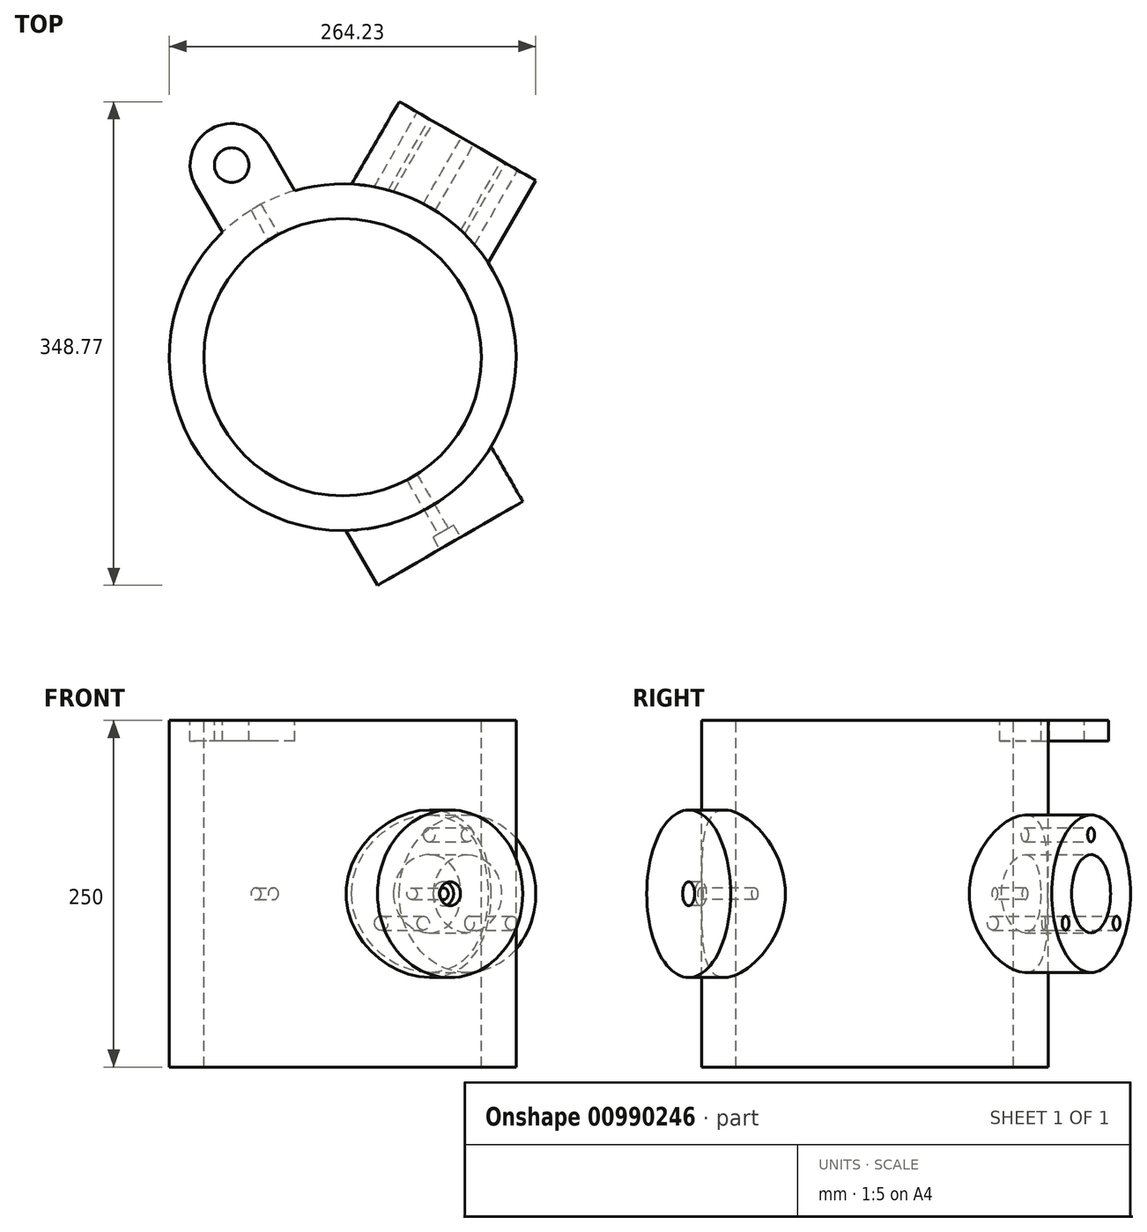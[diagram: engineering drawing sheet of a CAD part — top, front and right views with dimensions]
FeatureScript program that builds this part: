
annotation { "Feature Type Name" : "Feature", "Feature Type Description" : "" }
export const myFeature = defineFeature(function(context is Context, id is Id, definition is map)
    precondition{}
    {
        {
            var Q0;
            Q0=qCreatedBy(makeId("Top.planeOp"),FACE);
            cPlane(context, id + "F0", {"entities" : qUnion([Q0]), "cplaneType" : CPlaneType.OFFSET, "offset" : 125 * mm, "width" : 150 * mm, "height" : 150 * mm});
        }
        {
            var Q0;
            Q0=qCreatedBy(id+"F0.planeOp",FACE);
            var sketch = newSketch(context, id + "F1", { "sketchPlane" : qUnion([Q0])});
            skCircle(sketch, "E0", {"center": v(0, 0) * mm, "radius": 125 * mm});
            skCircle(sketch, "E1", {"center": v(0, 0) * mm, "radius": 100 * mm});
            skCircle(sketch, "E2", {"center": v(0, 0) * mm, "radius": 160 * mm, "construction": true});
            skSolve(sketch);
        }
        {
            var Q0;
            Q0 = qSketchRegion(id + "F1", true);
            extrude(context, id + "F2", {"entities" : qUnion([Q0]), "oppositeDirection" : true, "depth" : 250 * mm, "offsetDistance" : 25 * mm});
        }
        {
            var Q0;
            Q0=makeQuery(id+"F1.imprint","IMPRINT",FACE,{"disambiguationData":[TD([[makeQuery(id+"F1.imprint","IMPRINT",EDGE,{"derivedFrom":sQuery(id+"F1.wireOp",EDGE,"E0")}),1.0]])]});
            var sketch = newSketch(context, id + "F3", { "sketchPlane" : qUnion([Q0])});
            skLineSegment(sketch, "E3", {"start": v(0, 0) * mm, "end": v(-100, -173.2) * mm, "construction": true});
            skLineSegment(sketch, "E4", {"start": v(0, 0) * mm, "end": v(-105.59, 182.88) * mm, "construction": true});
            skLineSegment(sketch, "E5", {"start": v(0, 0) * mm, "end": v(211.08, 0) * mm, "construction": true});
            skLineSegment(sketch, "E6", {"start": v(-86.65, 90.09) * mm, "end": v(-105.98, 123.56) * mm});
            skArc(sketch, "E7", {"start": v(-105.98, 123.56) * mm, "mid": v(-94.98, 164.56) * mm, "end": v(-54, 153.53) * mm});
            skLineSegment(sketch, "E8.MirrorCS", {"start": v(-34.7, 120.09) * mm, "end": v(-54.02, 153.56) * mm});
            skCircle(sketch, "E9", {"center": v(-80, 138.56) * mm, "radius": 12.5 * mm});
            skLineSegment(sketch, "E10", {"start": v(0, 0) * mm, "end": v(-199.04, 0) * mm, "construction": true});
            skSolve(sketch);
        }
        {
            var Q0;
            {var subQ4=sQuery(id+"F3.wireOp",EDGE,"E6");Q0=makeQuery(id+"F3.imprint","IMPRINT",FACE,{"disambiguationData":[TD([[makeQuery(id+"F3.imprint","IMPRINT",EDGE,{"derivedFrom":subQ4}),-1.0]])]});}
            extrude(context, id + "F4", {"entities" : qUnion([Q0]), "operationType" : NewBodyOperationType.ADD, "oppositeDirection" : true, "depth" : 15 * mm, "offsetDistance" : 25 * mm});
        }
        {
            var Q0;
            Q0=sQuery(id+"F3.wireOp",EDGE,"E3");
            cPlane(context, id + "F5", {"entities" : qUnion([Q0]), "cplaneType" : CPlaneType.LINE_ANGLE, "offset" : 25 * mm, "angle" : 90 * degree, "width" : 150 * mm, "height" : 150 * mm});
        }
        {
            var Q0;
            Q0=qCreatedBy(makeId("Right.planeOp"),FACE);
            var sketch = newSketch(context, id + "F6", { "sketchPlane" : qUnion([Q0])});
            skLineSegment(sketch, "E11", {"start": v(0, 0) * mm, "end": v(0, -93.08) * mm, "construction": true});
            skSolve(sketch);
        }
        {
            var Q0;
            {var subQ0=sQuery(id+"F3.wireOp",EDGE,"E9");var subQ1=sQuery(id+"F3.wireOp",EDGE,"E8.MirrorCS");var subQ2=sQuery(id+"F3.wireOp",EDGE,"E7");var subQ3=sQuery(id+"F3.wireOp",EDGE,"E6");var subQ4=sQuery(id+"F1.wireOp",EDGE,"E0");Q0=makeQuery(id+"F7AuDATc02CG4dJ_1.1.F4.boolean.opBoolean","MERGE",FACE,{"derivedFrom":[makeQuery(id+"F7xKcid28HjBQqI_1.1.F4.boolean.opBoolean","MERGE",FACE,{"derivedFrom":[makeQuery(id+"F4.boolean.opBoolean","MERGE",FACE,{"derivedFrom":[makeQuery(id+"F2.opExtrude","CAP_FACE",FACE,{"disambiguationData":[OSD([subQ4,sQuery(id+"F1.wireOp",EDGE,"E1")])],"isStart":true}),makeQuery(id+"F4.opExtrude","CAP_FACE",FACE,{"disambiguationData":[OSD([subQ4,subQ3,subQ2,subQ1,subQ0])],"isStart":true})]}),makeQuery(id+"F7xKcid28HjBQqI_1.1.F4.opExtrude","CAP_FACE",FACE,{"disambiguationData":[OSD([subQ4,subQ3,subQ2,subQ1,subQ0])],"isStart":true})]}),makeQuery(id+"F7AuDATc02CG4dJ_1.1.F4.opExtrude","CAP_FACE",FACE,{"disambiguationData":[OSD([subQ4,subQ3,subQ2,subQ1,subQ0])],"isStart":true})]});}
            var sketch = newSketch(context, id + "F7", { "sketchPlane" : qUnion([Q0])});
            skPoint(sketch, "E12", {"position": v(160, 0) * mm});
            skLineSegment(sketch, "E13", {"start": v(-80, 138.56) * mm, "end": v(160, 0) * mm, "construction": true});
            skSolve(sketch);
        }
        {
            var Q0;
            Q0=sQuery(id+"F7.wireOp",EDGE,"E13");
            cPlane(context, id + "F8", {"entities" : qUnion([Q0]), "cplaneType" : CPlaneType.LINE_ANGLE, "offset" : 25 * mm, "angle" : 0 * degree, "width" : 150 * mm, "height" : 150 * mm});
        }
        {
            var Q0;
            Q0=qCreatedBy(id+"F8.planeOp",FACE);
            cPlane(context, id + "F9", {"entities" : qUnion([Q0]), "cplaneType" : CPlaneType.OFFSET, "offset" : 100 * mm, "width" : 150 * mm, "height" : 150 * mm});
        }
        {
            var Q0;
            Q0=qCreatedBy(id+"F9.planeOp",FACE);
            var sketch = newSketch(context, id + "F10", { "sketchPlane" : qUnion([Q0])});
            skCircle(sketch, "E14", {"center": v(0, 0) * mm, "radius": 56.85 * mm});
            skCircle(sketch, "E15", {"center": v(0, 0) * mm, "radius": 28.16 * mm});
            skCircle(sketch, "E16", {"center": v(0, 42.47) * mm, "radius": 5 * mm});
            skCircle(sketch, "E17", {"center": v(0, 0) * mm, "radius": 42.47 * mm, "construction": true});
            skLineSegment(sketch, "E18", {"start": v(0, 42.47) * mm, "end": v(0, 0) * mm, "construction": true});
            skLineSegment(sketch, "E19", {"start": v(0, 0) * mm, "end": v(36.78, -21.23) * mm, "construction": true});
            skLineSegment(sketch, "E20", {"start": v(36.78, -21.23) * mm, "end": v(0, 0) * mm, "construction": true});
            skLineSegment(sketch, "E21", {"start": v(0, 0) * mm, "end": v(-36.78, -21.23) * mm, "construction": true});
            skCircle(sketch, "E22.1.0", {"center": v(-36.78, -21.23) * mm, "radius": 5 * mm});
            skLineSegment(sketch, "E22.1.1", {"start": v(-36.78, -21.23) * mm, "end": v(0, 0) * mm, "construction": true});
            skCircle(sketch, "E22.2.0", {"center": v(36.78, -21.23) * mm, "radius": 5 * mm});
            skSolve(sketch);
        }
        {
            var Q0;
            Q0 = qSketchRegion(id + "F10", true);
            extrude(context, id + "F11", {"entities" : qUnion([Q0]), "operationType" : NewBodyOperationType.ADD, "surfaceOperationType" : NewSurfaceOperationType.ADD, "endBound" : BoundingType.UP_TO_NEXT, "oppositeDirection" : true, "depth" : 112 * mm, "offsetDistance" : 25 * mm});
        }
        {
            var Q0;
            {var subQ6=sQuery(id+"F1.wireOp",EDGE,"E1");Q0=makeQuery(id+"F7.imprint","IMPRINT",FACE,{"disambiguationData":[TD([[makeQuery(id+"F7.imprint","IMPRINT",EDGE,{"derivedFrom":makeQuery(id+"F2.opExtrude","CAP_EDGE",EDGE,{"disambiguationData":[OSD([subQ6])],"isStart":true})}),-1.0]])]});}
            var sketch = newSketch(context, id + "F12", { "sketchPlane" : qUnion([Q0])});
            skPoint(sketch, "E23", {"position": v(-80, -138.56) * mm});
            skLineSegment(sketch, "E24", {"start": v(-80, -138.56) * mm, "end": v(160, 0) * mm, "construction": true});
            skSolve(sketch);
        }
        {
            var Q0;
            Q0=sQuery(id+"F12.wireOp",EDGE,"E24");
            cPlane(context, id + "F13", {"entities" : qUnion([Q0]), "cplaneType" : CPlaneType.LINE_ANGLE, "offset" : 25 * mm, "angle" : 0 * degree, "width" : 150 * mm, "height" : 150 * mm});
        }
        {
            var Q0;
            Q0=qCreatedBy(id+"F13.planeOp",FACE);
            cPlane(context, id + "F14", {"entities" : qUnion([Q0]), "cplaneType" : CPlaneType.OFFSET, "offset" : 75 * mm, "oppositeDirection" : true, "width" : 150 * mm, "height" : 150 * mm});
        }
        {
            var Q0;
            Q0=qCreatedBy(id+"F14.planeOp",FACE);
            var sketch = newSketch(context, id + "F15", { "sketchPlane" : qUnion([Q0])});
            skCircle(sketch, "E25", {"center": v(0, 0) * mm, "radius": 60.45 * mm});
            skSolve(sketch);
        }
        {
            var Q0;
            Q0 = qSketchRegion(id + "F15", true);
            extrude(context, id + "F16", {"entities" : qUnion([Q0]), "operationType" : NewBodyOperationType.ADD, "endBound" : BoundingType.UP_TO_NEXT, "depth" : 25 * mm, "offsetDistance" : 25 * mm});
        }
        {
            var Q0;
            Q0=makeQuery(id+"F16.opExtrude","CAP_FACE",FACE,{"disambiguationData":[OSD([sQuery(id+"F15.wireOp",EDGE,"E25")])],"isStart":true});
            var sketch = newSketch(context, id + "F17", { "sketchPlane" : qUnion([Q0])});
            skPoint(sketch, "E26", {"position": v(0, 0) * mm});
            skSolve(sketch);
        }
        {
            var Q0;
            Q0=sQuery(id+"F17.wireOp",VERTEX,"E26");
            var Q1;
            Q1=makeQuery(id+"F2.opExtrude","SWEPT_BODY",BODY,{"disambiguationData":[OSD([sQuery(id+"F1.wireOp",EDGE,"E0"),sQuery(id+"F1.wireOp",EDGE,"E1")])]});
            hole(context, id + "F18", {"style" : HoleStyle.C_BORE, "endStyle" : HoleEndStyle.THROUGH, "standardTappedOrClearance" : lookupTablePath({ "standard" : "ISO", "engagement" : "75%", "pitch" : "1.5 mm", "size" : "M10", "type" : "Tapped" }), "standardBlindInLast" : lookupTablePath({ "standard" : "ISO", "fit" : "Normal", "engagement" : "75%", "pitch" : "1.5 mm", "size" : "M10", "type" : "Clearance & tapped" }), "holeDiameter" : 8.5 * mm, "cBoreDiameter" : 17.25 * mm, "cBoreDepth" : 10 * mm, "majorDiameter" : 10 * mm, "showTappedDepth" : true, "isTappedThrough" : true, "tappedDepth" : 12 * mm, "tapClearance" : 3, "startFromSketch" : true, "locations" : qUnion([Q0]), "scope" : qUnion([Q1])});
        }
    });
